# Revit family: Jamolite II
name_source: partatom
category: Doors
revit_build: Autodesk Revit 2014 (Build: 20140709_2115(x64)
units: mm (PartAtom-declared; Revit-internal decimal feet)

## types (13) — shared parameters
Analytic Construction = <None>
Closure Offset = 8"
DOOR CLOSER = 14"
Frame = <By Category>
Frame Projection Ext. = 1"
Frame Projection Int. = 1"
Frame Width = 3"
Function = Interior
Height = 84"
LATCH STRIKE TAPPING BAR = 41"
Shutter = <By Category>
Wall Closure = By host
Width = 36"

## per-type parameters (varying)
| type | Buck Opening | Buck Opening HT. | HIC | Rough Height | Rough Width | Thickness | WIC |
| 2'6"X6'6"X4" | 30" | 78" | 76" | 78" | 30 3/4" | 4" | 26" |
| 2'6"X6'6"X6" | 30" | 78" | 76" | 78" | 30 3/4" | 6" | 26" |
| 3'0" X 6'6"X 4" | 36" | 78" | 76" | 78" | 36 3/4" | 6" | 32" |
| 3'6" X 6'6"X 4" | 42" | 78" | 76" | 78" | 42 3/4" | 4" | 38" |
| 3'6" X 6'6"X 6" | 42" | 78" | 76" | 78" | 42 3/4" | 6" | 38" |
| 4'0" X 6'6"X 4" | 48" | 78" | 76" | 78" | 48 3/4" | 6" | 44" |
| 4'6" X 6'6"X 4" | 54" | 78" | 76" | 78" | 54 3/4" | 4" | 50" |
| 5'0" X 6'6"X 4" | 60" | 78" | 76" | 78" | 60 3/4" | 4" | 56" |
| 3'0" X 7'0"X 4" | 36" | 84" | 82" | 84" | 36 3/4" | 4" | 32" |
| 3'0" X 7'0"X 6" | 36" | 84" | 82" | 84" | 36 3/4" | 6" | 32" |
| 3'6" X 7'0"X 4" | 42" | 84" | 82" | 84" | 42 3/4" | 6" | 38" |
| 5'0" X 7'0"X 4" | 60" | 84" | 82" | 84" | 60 3/4" | 4" | 56" |
| 5'0" X 7'0"X 6" | 60" | 84" | 82" | 84" | 60 3/4" | 6" | 56" |

## geometry (parser evidence)
native form markers: Sweep x42
no freeform markers — native parametric forms only
